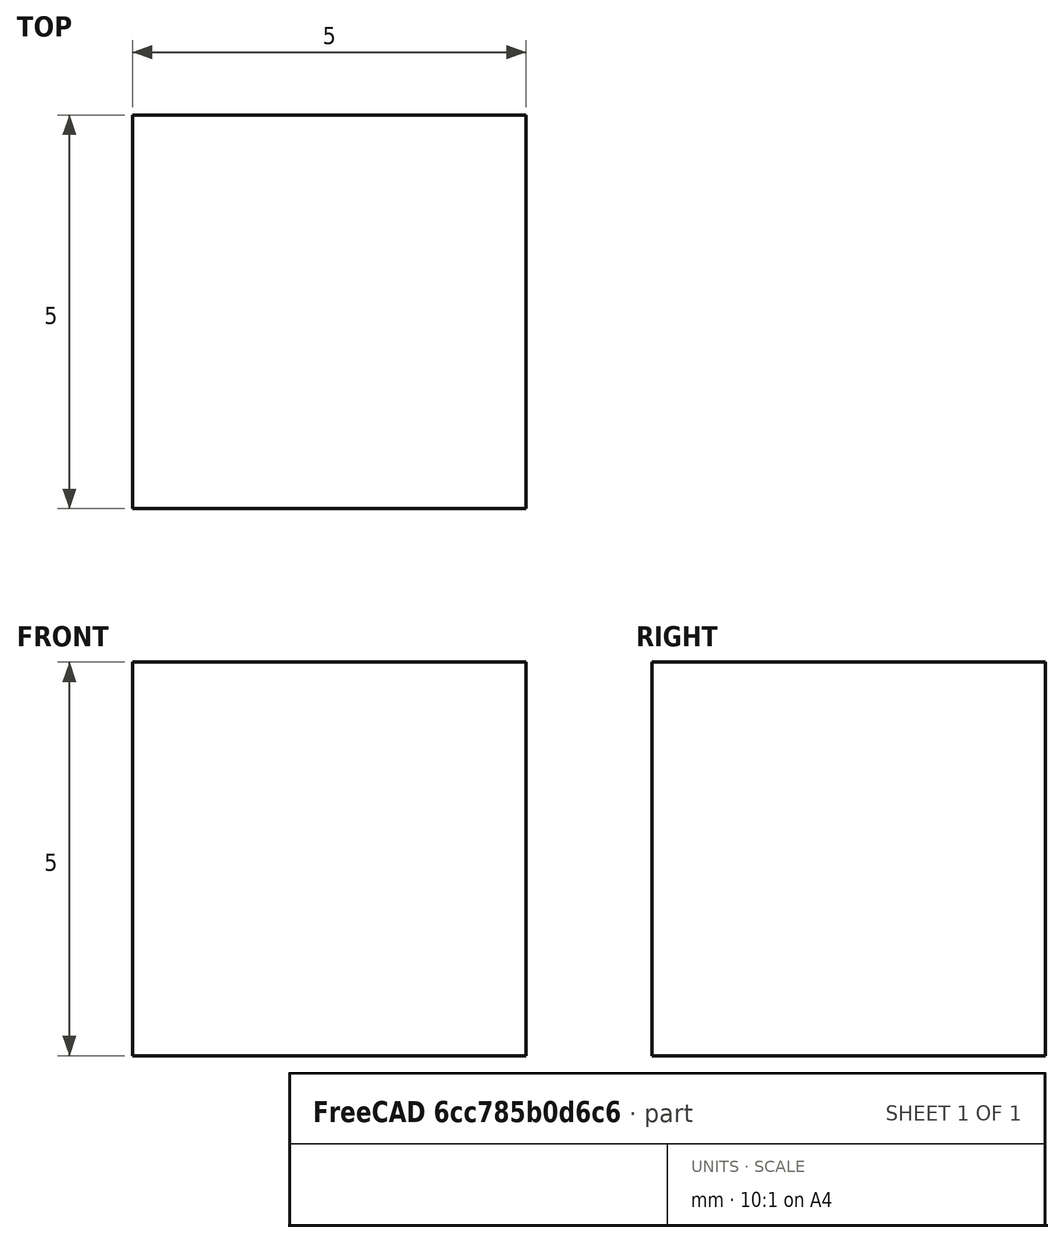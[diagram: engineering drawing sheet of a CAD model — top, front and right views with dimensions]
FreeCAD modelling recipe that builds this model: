
FCSTD DOCUMENT  (FreeCAD 0.18.4R)
Label: cannon-support-pin
License: All rights reserved
LicenseURL: http://en.wikipedia.org/wiki/All_rights_reserved
objects: Sketcher::SketchObject×1, PartDesign::Pad×1, PartDesign::Body×1
note: 4 computed .brp shape members not serialized (recipe doc carries the construction recipe); baked Part::Feature solids carry a one-line shape summary decoded from their .brp

FEATURE [Sketcher::SketchObject] Sketch
  MapMode = 5
  Placement = pos=(0,0,0) rot=(1,0,0;1.5708rad)
  Support = -> [XZ_Plane]
  sketch-geometry (4):
    g0: LineSegment StartX=-2.5 StartY=2.5 StartZ=0 EndX=2.5 EndY=2.5 EndZ=0
    g1: LineSegment StartX=2.5 StartY=2.5 StartZ=0 EndX=2.5 EndY=-2.5 EndZ=0
    g2: LineSegment StartX=2.5 StartY=-2.5 StartZ=0 EndX=-2.5 EndY=-2.5 EndZ=0
    g3: LineSegment StartX=-2.5 StartY=-2.5 StartZ=0 EndX=-2.5 EndY=2.5 EndZ=0
  constraints (12):
    c: Coincident(g0,g1)
    c: Coincident(g1,g2)
    c: Coincident(g2,g3)
    c: Coincident(g3,g0)
    c: Horizontal(g0)
    c: Horizontal(g2)
    c: Vertical(g1)
    c: Vertical(g3)
    c: DistanceX(g2,g2) = 5
    c: Equal(g3,g2)
    c: DistanceX(g0,g-1) = 2.5
    c: DistanceY(g2,g-1) = 2.5
FEATURE [PartDesign::Pad] Pad
  Length = 5
  Length2 = 100
  Placement = pos=(0,0,0) rot=(1,0,0;1.5708rad)
  Profile = -> Sketch
  Type = 0
FEATURE [PartDesign::Body] Body
  Group = -> [Sketch,Pad]
  Origin = -> Origin
  Tip = -> Pad
